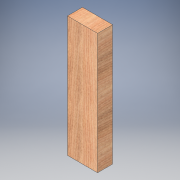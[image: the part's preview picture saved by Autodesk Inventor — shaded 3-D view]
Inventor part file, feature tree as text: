
AUTODESK INVENTOR PART (.ipt)
format: ipt  version: 2017 (Build 210142000, 142)  size: 110,080 bytes
history: native  units: in
note: dims shown in document units (in); Inventor stores cm internally (conversion verified against a paired STEP export)
features: extrude x1, sketch x1
ambient origin geometry x8: Origin, YZ Plane, XZ Plane, XY Plane, X Axis, Y Axis, Z Axis, Center Point
bodies: Solid1 (feature_tree)
feature tree (2):
  extrude  "Extrusion1"  Depth=24.0in
  sketch  "Sketch1"  dims[d0=6.0in d1=24.0in d2=3.0in d3=0.0in]
